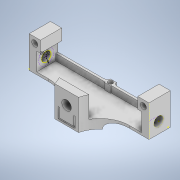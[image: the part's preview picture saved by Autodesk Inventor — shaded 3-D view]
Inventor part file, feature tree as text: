
AUTODESK INVENTOR PART (.ipt)
format: ipt  version: 2020.1 (Build 241239000, 239)  size: 411,648 bytes
history: native  units: mm
features: sketch x38, extrude x22, fillet x6
ambient origin geometry x8: Origin, YZ Plane, XZ Plane, XY Plane, X Axis, Y Axis, Z Axis, Center Point
bodies: Solid1 (feature_tree)
feature tree (66):
  sketch  "Sketch1"  dims[d3=25.4mm d4=25.4mm]
  extrude  "Extrusion1"  Depth=25.4mm
  extrude  "Extrusion2"  Depth=10.0mm TaperAngle=0.0deg
  extrude  "Extrusion3"  Depth=15.0mm
  sketch  "Sketch6"  dims[d14=14.85mm d15=0.0mm d16=20.32mm]
  extrude  "Extrusion4"  Depth=25.4mm TaperAngle=0.0deg
  sketch  "Sketch8"  dims[d20=150.0mm d21=10.0mm d22=0.0mm d23=0.0mm d24=10.0mm d25=0.0mm]
  extrude  "Extrusion5"  Depth=20.32mm
  extrude  "Extrusion6"  Depth=3.25mm
  sketch  "Sketch11"  dims[d31=18.0mm d32=25.4mm d33=0.0mm]
  extrude  "Extrusion7"  Depth=10.0mm TaperAngle=0.0deg
  extrude  "Extrusion8"  Depth=15.0mm
  extrude  "Extrusion9"  Depth=25.4mm TaperAngle=0.0deg
  sketch  "Sketch14"  dims[d40=20.0mm d41=0.0mm d42=25.0mm]
  sketch  "Sketch15"  dims[d43=10.0mm d44=0.0mm d45=31.75mm]
  sketch  "Sketch16"  dims[d46=10.0mm d47=0.0mm d48=12.7mm d49=10.0mm d50=0.0mm]
  extrude  "Extrusion10"  Depth=25.4mm TaperAngle=0.0deg
  extrude  "Extrusion11"  Depth=14.9mm TaperAngle=0.0deg
  sketch  "Sketch19"  dims[d66=15.0mm d67=0.0mm d68=9.0mm]
  sketch  "Sketch20"  dims[d71=3.0mm d72=0.0mm d73=2.5mm]
  extrude  "Extrusion12"  Depth=31.75mm
  extrude  "Extrusion13"  Depth=25.0mm
  sketch  "Sketch23"  dims[d80=3.0mm d81=0.0mm d82=6.25mm d83=8.0mm]
  extrude  "Extrusion14"  Depth=10.0mm
  extrude  "Extrusion15"  Depth=10.0mm
  fillet  "Fillet1"  Radius=10.0mm
  sketch  "Sketch26"  dims[d85=11.75mm d86=0.0mm]
  sketch  "Sketch27"  dims[d87=12.0mm d88=0.0mm]
  sketch  "Sketch28"  dims[d89=5.0mm]
  sketch  "Sketch29"  dims[d90=0.502mm d91=0.0mm]
  extrude  "Extrusion16"  Depth=1.5875mm
  sketch  "Sketch31"  dims[d94=39.25mm]
  sketch  "Sketch32"
  extrude  "Extrusion17"  Depth=1.5875mm
  fillet  "Fillet2"  Radius=6.35mm
  fillet  "Fillet3"  Radius=8.0mm
  fillet  "Fillet4"  Radius=20.0mm
  sketch  "Sketch34"
  extrude  "Extrusion18"  Depth=9.0mm
  sketch  "Sketch36"
  extrude  "Extrusion19"  Depth=2.5mm
  extrude  "Extrusion20"  Depth=3.0mm TaperAngle=0.0deg
  fillet  "Fillet5"  Radius=0.5mm
  extrude  "Extrusion21"  Depth=1.0mm
  extrude  "Extrusion22"  Depth=6.25mm
  fillet  "Fillet6"  Radius=8.0mm
  sketch  "Sketch2"  dims[d5=12.7mm d6=10.0mm d7=0.0mm]
  sketch  "Sketch3"  dims[d8=15.0mm d9=15.0mm]
  sketch  "Sketch4"  dims[d10=8.0mm d11=25.4mm d12=0.0mm]
  sketch  "Sketch7"  dims[d18=2.0mm d19=3.25mm]
  sketch  "Sketch9"  dims[d26=15.0mm d27=15.0mm]
  sketch  "Sketch10"  dims[d28=8.0mm d29=25.4mm d30=0.0mm]
  sketch  "Sketch12"  dims[d34=7.4mm d35=14.9mm d36=0.0mm]
  sketch  "Sketch13"  dims[d37=14.9mm d38=0.0mm d39=31.75mm]
  sketch  "Sketch17"  dims[d51=21.0mm d58=1.5875mm]
  sketch  "Sketch18"  dims[d59=1.5875mm d60=1.5875mm d61=6.35mm d63=8.0mm d64=20.0mm d65=0.0mm]
  sketch  "Sketch21"  dims[d74=2.5mm d75=3.0mm d76=0.0mm d77=0.5mm]
  sketch  "Sketch22"  dims[d78=1.0mm d79=1.0mm]
  sketch  "Sketch25"  dims[d84=8.0mm]
  sketch  "Sketch30"  dims[d92=1.0mm d93=0.0mm]
  sketch  "Sketch33"
  sketch  "Sketch35"
  sketch  "Sketch37"
  sketch  "Sketch38"
  sketch  "Sketch39"
  sketch  "Sketch40"
